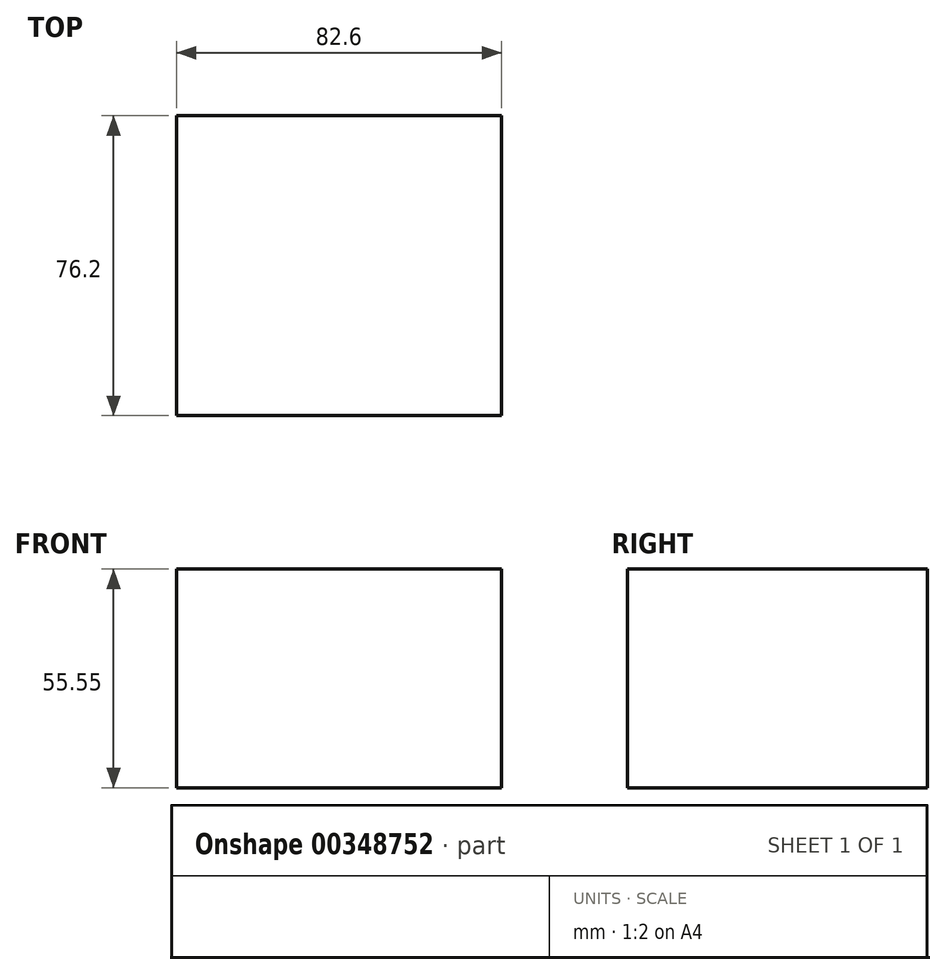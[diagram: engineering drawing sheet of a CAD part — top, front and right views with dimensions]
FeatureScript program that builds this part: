
annotation { "Feature Type Name" : "Feature", "Feature Type Description" : "" }
export const myFeature = defineFeature(function(context is Context, id is Id, definition is map)
    precondition{}
    {
        {
            var Q0;
            Q0=qCreatedBy(makeId("Front.planeOp"),FACE);
            var sketch = newSketch(context, id + "F0", { "sketchPlane" : qUnion([Q0])});
            skLineSegment(sketch, "E0.bottom", {"start": v(-47.49, 33.1) * mm, "end": v(35.11, 33.1) * mm});
            skLineSegment(sketch, "E0.top", {"start": v(-47.49, -22.45) * mm, "end": v(35.11, -22.45) * mm});
            skLineSegment(sketch, "E0.left", {"start": v(-47.49, 33.1) * mm, "end": v(-47.49, -22.45) * mm});
            skLineSegment(sketch, "E0.right", {"start": v(35.11, 33.1) * mm, "end": v(35.11, -22.45) * mm});
            skSolve(sketch);
        }
        {
            var Q0;
            Q0=makeQuery(id+"F0.imprint","IMPRINT",FACE,{"disambiguationData":[TD([[makeQuery(id+"F0.imprint","IMPRINT",EDGE,{"derivedFrom":sQuery(id+"F0.wireOp",EDGE,"E0.bottom")}),-1.0]])]});
            extrude(context, id + "F1", {"entities" : qUnion([Q0]), "depth" : 76.2 * mm});
        }
    });
